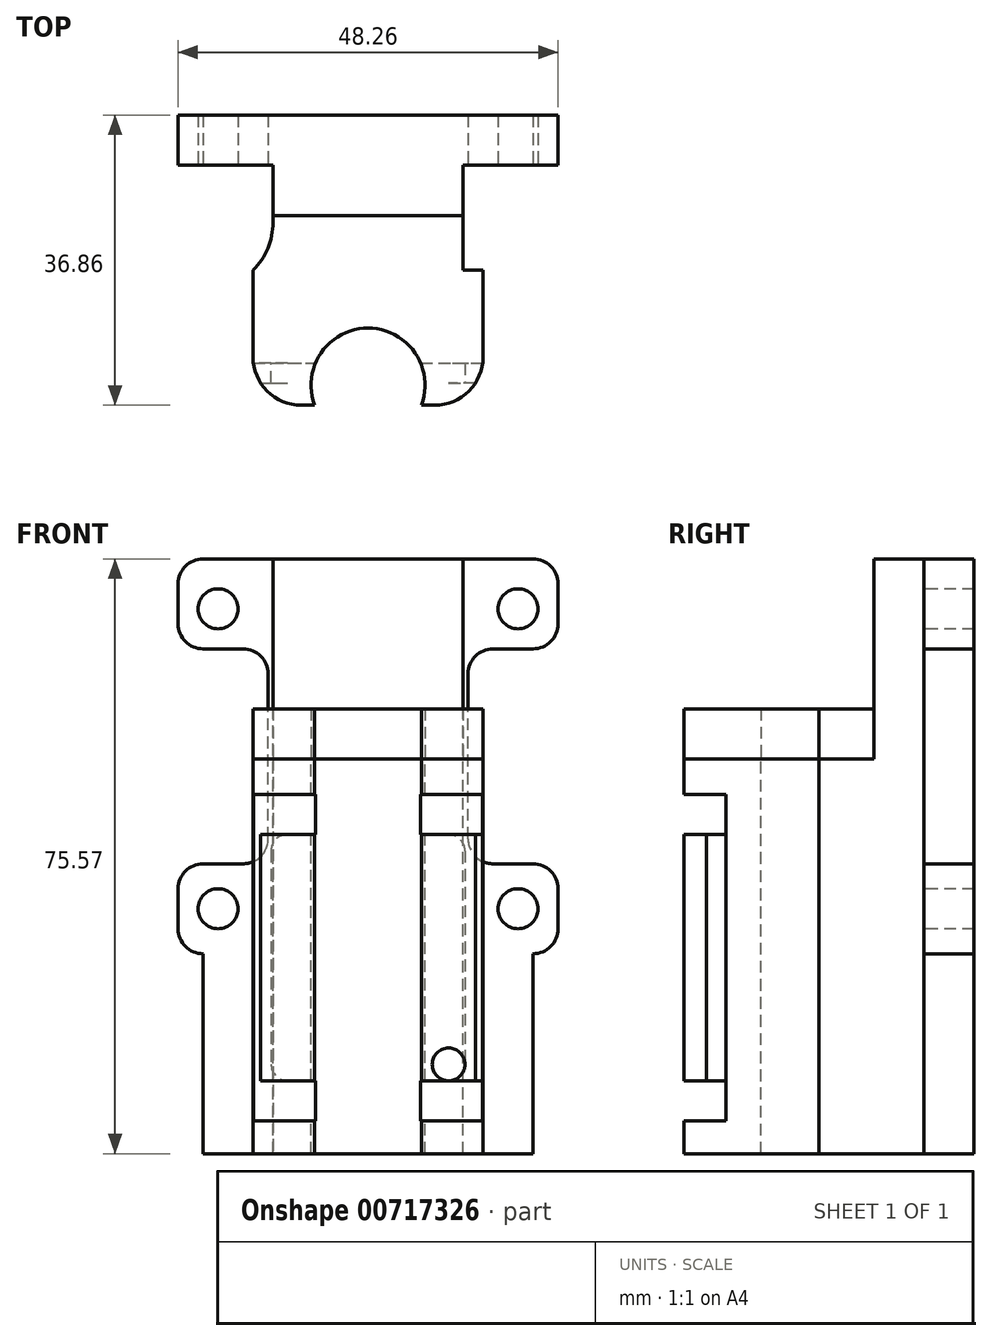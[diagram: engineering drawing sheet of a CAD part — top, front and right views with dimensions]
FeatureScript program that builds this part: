
annotation { "Feature Type Name" : "Feature", "Feature Type Description" : "" }
export const myFeature = defineFeature(function(context is Context, id is Id, definition is map)
    precondition{}
    {
        {
            var Q0;
            Q0=qCreatedBy(makeId("Front.planeOp"),FACE);
            var sketch = newSketch(context, id + "F0", { "sketchPlane" : qUnion([Q0])});
            skLineSegment(sketch, "E0.bottom", {"start": v(14.6, -25.4) * mm, "end": v(-14.6, -25.4) * mm});
            skLineSegment(sketch, "E0.top", {"start": v(14.6, 25.4) * mm, "end": v(-14.6, 25.4) * mm});
            skLineSegment(sketch, "E0.left", {"start": v(14.6, -25.4) * mm, "end": v(14.6, 25.4) * mm});
            skLineSegment(sketch, "E0.right", {"start": v(-14.6, -25.4) * mm, "end": v(-14.6, 25.4) * mm});
            skPoint(sketch, "E0.middle", {"position": v(0, 0) * mm});
            skSolve(sketch);
        }
        {
            var Q0;
            Q0=makeQuery(id+"F0.imprint","IMPRINT",FACE,{"disambiguationData":[TD([[makeQuery(id+"F0.imprint","IMPRINT",EDGE,{"derivedFrom":sQuery(id+"F0.wireOp",EDGE,"E0.bottom")}),-1.0]])]});
            extrude(context, id + "F1", {"entities" : qUnion([Q0]), "depth" : 1.65 * mm, "offsetDistance" : 25.4 * mm});
        }
        {
            var Q0;
            Q0=makeQuery(id+"F1.opExtrude","CAP_FACE",FACE,{"disambiguationData":[OSD([sQuery(id+"F0.wireOp",EDGE,"E0.bottom"),sQuery(id+"F0.wireOp",EDGE,"E0.top"),sQuery(id+"F0.wireOp",EDGE,"E0.left"),sQuery(id+"F0.wireOp",EDGE,"E0.right")])],"isStart":false});
            var sketch = newSketch(context, id + "F2", { "sketchPlane" : qUnion([Q0])});
            skLineSegment(sketch, "E1.bottom", {"start": v(14.6, -25.4) * mm, "end": v(-14.6, -25.4) * mm});
            skLineSegment(sketch, "E1.top", {"start": v(14.6, 25.4) * mm, "end": v(-14.6, 25.4) * mm});
            skLineSegment(sketch, "E1.left", {"start": v(14.6, -25.4) * mm, "end": v(14.6, 25.4) * mm});
            skLineSegment(sketch, "E1.right", {"start": v(-14.6, -25.4) * mm, "end": v(-14.6, 25.4) * mm});
            skPoint(sketch, "E1.middle", {"position": v(0, 0) * mm});
            skSolve(sketch);
        }
        {
            var Q0;
            Q0=qSketchRegion(id+"F2",true);
            extrude(context, id + "F3", {"entities" : qUnion([Q0]), "operationType" : NewBodyOperationType.ADD, "depth" : 5.33 * mm, "offsetDistance" : 25.4 * mm});
        }
        {
            var Q0;
            Q0=makeQuery(id+"F3.opExtrude","CAP_FACE",FACE,{"disambiguationData":[OSD([sQuery(id+"F2.wireOp",EDGE,"E1.bottom"),sQuery(id+"F2.wireOp",EDGE,"E1.top"),sQuery(id+"F2.wireOp",EDGE,"E1.left"),sQuery(id+"F2.wireOp",EDGE,"E1.right")])],"isStart":false});
            var sketch = newSketch(context, id + "F4", { "sketchPlane" : qUnion([Q0])});
            skLineSegment(sketch, "E2.bottom", {"start": v(14.6, -25.4) * mm, "end": v(-14.6, -25.4) * mm});
            skLineSegment(sketch, "E2.top", {"start": v(14.6, 25.4) * mm, "end": v(-14.6, 25.4) * mm});
            skLineSegment(sketch, "E2.left", {"start": v(14.6, -25.4) * mm, "end": v(14.6, 25.4) * mm});
            skLineSegment(sketch, "E2.right", {"start": v(-14.6, -25.4) * mm, "end": v(-14.6, 25.4) * mm});
            skPoint(sketch, "E2.middle", {"position": v(0, 0) * mm});
            skSolve(sketch);
        }
        {
            var Q0;
            Q0=makeQuery(id+"F4.imprint","IMPRINT",FACE,{"disambiguationData":[TD([[makeQuery(id+"F4.imprint","IMPRINT",EDGE,{"derivedFrom":sQuery(id+"F4.wireOp",EDGE,"E2.bottom")}),-1.0]])]});
            extrude(context, id + "F5", {"entities" : qUnion([Q0]), "operationType" : NewBodyOperationType.ADD, "depth" : 10.16 * mm, "offsetDistance" : 25.4 * mm});
        }
        {
            var Q0;
            Q0=makeQuery(id+"F5.boolean.opBoolean","MERGE",FACE,{"derivedFrom":[makeQuery(id+"F3.boolean.opBoolean","MERGE",FACE,{"derivedFrom":[makeQuery(id+"F1.opExtrude","SWEPT_FACE",FACE,{"disambiguationData":[OSD([sQuery(id+"F0.wireOp",EDGE,"E0.top")])]}),makeQuery(id+"F3.opExtrude","SWEPT_FACE",FACE,{"disambiguationData":[OSD([sQuery(id+"F2.wireOp",EDGE,"E1.top")])]})]}),makeQuery(id+"F5.opExtrude","SWEPT_FACE",FACE,{"disambiguationData":[OSD([sQuery(id+"F4.wireOp",EDGE,"E2.top")])]})]});
            var sketch = newSketch(context, id + "F6", { "sketchPlane" : qUnion([Q0])});
            skCircle(sketch, "E3", {"center": v(0, -14.59) * mm, "radius": 7.24 * mm});
            skSolve(sketch);
        }
        {
            var Q0;
            Q0=makeQuery(id+"F6.imprint","IMPRINT",FACE,{"disambiguationData":[TD([[makeQuery(id+"F6.imprint","IMPRINT",EDGE,{"derivedFrom":sQuery(id+"F6.wireOp",EDGE,"E3")}),1.0]])]});
            extrude(context, id + "F7", {"entities" : qUnion([Q0]), "operationType" : NewBodyOperationType.REMOVE, "oppositeDirection" : true, "depth" : 54.6 * mm, "offsetDistance" : 25.4 * mm});
        }
        {
            var Q0;
            Q0=makeQuery(id+"F5.opExtrude","CAP_EDGE",EDGE,{"disambiguationData":[OSD([sQuery(id+"F4.wireOp",EDGE,"E2.left")])],"isStart":false});
            var Q1;
            Q1=makeQuery(id+"F5.opExtrude","CAP_EDGE",EDGE,{"disambiguationData":[OSD([sQuery(id+"F4.wireOp",EDGE,"E2.right")])],"isStart":false});
            fillet(context, id + "F8", {"entities" : qUnion([Q0, Q1]), "radius" : 6.13 * mm, "tangentPropagation" : true, "allowEdgeOverflow" : false});
        }
        {
            var Q0;
            Q0=makeQuery(id+"F1.opExtrude","CAP_FACE",FACE,{"disambiguationData":[OSD([sQuery(id+"F0.wireOp",EDGE,"E0.bottom"),sQuery(id+"F0.wireOp",EDGE,"E0.top"),sQuery(id+"F0.wireOp",EDGE,"E0.left"),sQuery(id+"F0.wireOp",EDGE,"E0.right")])],"isStart":true});
            var sketch = newSketch(context, id + "F9", { "sketchPlane" : qUnion([Q0])});
            skLineSegment(sketch, "E4.bottom", {"start": v(-12.07, -25.4) * mm, "end": v(12.07, -25.4) * mm});
            skLineSegment(sketch, "E4.top", {"start": v(-12.07, 25.4) * mm, "end": v(12.07, 25.4) * mm});
            skLineSegment(sketch, "E4.left", {"start": v(-12.07, -25.4) * mm, "end": v(-12.07, 25.4) * mm});
            skLineSegment(sketch, "E4.right", {"start": v(12.07, -25.4) * mm, "end": v(12.07, 25.4) * mm});
            skPoint(sketch, "E4.middle", {"position": v(0, 0) * mm});
            skSolve(sketch);
        }
        {
            var Q0;
            Q0=makeQuery(id+"F9.imprint","IMPRINT",FACE,{"disambiguationData":[TD([[makeQuery(id+"F9.imprint","IMPRINT",EDGE,{"derivedFrom":sQuery(id+"F9.wireOp",EDGE,"E4.bottom")}),1.0]])]});
            extrude(context, id + "F10", {"entities" : qUnion([Q0]), "operationType" : NewBodyOperationType.ADD, "depth" : 13.36 * mm, "offsetDistance" : 25.4 * mm});
        }
        {
            var Q0;
            Q0=makeQuery(id+"F10.opExtrude","CAP_FACE",FACE,{"disambiguationData":[OSD([sQuery(id+"F0.wireOp",EDGE,"E0.bottom"),sQuery(id+"F0.wireOp",EDGE,"E0.top"),sQuery(id+"F0.wireOp",EDGE,"E0.left"),sQuery(id+"F0.wireOp",EDGE,"E0.right"),sQuery(id+"FqzVllP4adCt4uL_1.wireOp",EDGE,"rUKK4DPj-CFjB-32sL-ua7b-D3d8OQX9hJPr"),sQuery(id+"FqzVllP4adCt4uL_1.wireOp",EDGE,"QhqLk9Nw-JTsH-iBzY-8FqU-bG79tKQu5XAJ"),sQuery(id+"FqzVllP4adCt4uL_1.wireOp",EDGE,"1LGBsUpi-39JT-yavD-d9wK-DNn5E7mbPaeu"),sQuery(id+"FqzVllP4adCt4uL_1.wireOp",EDGE,"ZftcWFY4-HbeK-KcCb-HpW3-OdhueiSprC3Z"),sQuery(id+"F9.wireOp",EDGE,"E4.bottom"),sQuery(id+"F9.wireOp",EDGE,"E4.top"),sQuery(id+"F9.wireOp",EDGE,"E4.left"),sQuery(id+"F9.wireOp",EDGE,"E4.right")])],"isStart":false});
            var sketch = newSketch(context, id + "F11", { "sketchPlane" : qUnion([Q0])});
            skLineSegment(sketch, "E5", {"start": v(12.7, -25.4) * mm, "end": v(6.35, -25.4) * mm});
            skLineSegment(sketch, "E6", {"start": v(12.7, -25.4) * mm, "end": v(20.95, -25.4) * mm});
            skLineSegment(sketch, "E7", {"start": v(24.13, -22.23) * mm, "end": v(24.13, -17.14) * mm});
            skLineSegment(sketch, "E8", {"start": v(11.1, 24.77) * mm, "end": v(-11.12, 24.77) * mm});
            skLineSegment(sketch, "E9", {"start": v(-6.35, -25.4) * mm, "end": v(-12.7, -25.4) * mm});
            skLineSegment(sketch, "E10", {"start": v(-12.7, -25.4) * mm, "end": v(-20.96, -25.4) * mm});
            skLineSegment(sketch, "E11", {"start": v(-24.13, 21.59) * mm, "end": v(-24.13, 16.51) * mm});
            skLineSegment(sketch, "E12", {"start": v(-6.35, 8.9) * mm, "end": v(-6.35, -25.4) * mm});
            skLineSegment(sketch, "E13", {"start": v(-6.35, 24.77) * mm, "end": v(-6.35, 8.9) * mm});
            skLineSegment(sketch, "E14", {"start": v(6.35, 24.77) * mm, "end": v(6.35, 8.9) * mm});
            skLineSegment(sketch, "E15", {"start": v(6.35, -25.4) * mm, "end": v(6.35, 8.9) * mm});
            skLineSegment(sketch, "E16", {"start": v(-6.35, -25.4) * mm, "end": v(6.35, -25.4) * mm});
            skLineSegment(sketch, "E17", {"start": v(12.7, -10.8) * mm, "end": v(12.7, 10.16) * mm});
            skLineSegment(sketch, "E18", {"start": v(-12.7, -10.8) * mm, "end": v(-12.7, 10.16) * mm});
            skLineSegment(sketch, "E19", {"start": v(15.87, -13.97) * mm, "end": v(20.95, -13.97) * mm});
            skLineSegment(sketch, "E20", {"start": v(20.95, 13.34) * mm, "end": v(15.87, 13.34) * mm});
            skLineSegment(sketch, "E21", {"start": v(-15.88, -13.97) * mm, "end": v(-20.96, -13.97) * mm});
            skLineSegment(sketch, "E22", {"start": v(-15.88, 13.34) * mm, "end": v(-20.96, 13.34) * mm});
            skLineSegment(sketch, "E23", {"start": v(-24.13, -17.14) * mm, "end": v(-24.13, -22.23) * mm});
            skLineSegment(sketch, "E24", {"start": v(24.13, 21.59) * mm, "end": v(24.13, 16.51) * mm});
            skArc(sketch, "E25", {"start": v(-12.7, 10.16) * mm, "mid": v(-13.63, 12.4) * mm, "end": v(-15.88, 13.34) * mm});
            skArc(sketch, "E26", {"start": v(-15.88, -13.97) * mm, "mid": v(-13.63, -13.04) * mm, "end": v(-12.7, -10.8) * mm});
            skArc(sketch, "E27", {"start": v(15.87, 13.34) * mm, "mid": v(13.63, 12.4) * mm, "end": v(12.7, 10.16) * mm});
            skArc(sketch, "E28", {"start": v(12.7, -10.8) * mm, "mid": v(13.63, -13.04) * mm, "end": v(15.87, -13.97) * mm});
            skArc(sketch, "E29", {"start": v(24.13, 21.59) * mm, "mid": v(23.2, 23.84) * mm, "end": v(20.95, 24.77) * mm});
            skArc(sketch, "E30", {"start": v(20.95, 13.34) * mm, "mid": v(23.2, 14.26) * mm, "end": v(24.13, 16.51) * mm});
            skArc(sketch, "E31", {"start": v(24.13, -17.14) * mm, "mid": v(23.2, -14.9) * mm, "end": v(20.95, -13.97) * mm});
            skArc(sketch, "E32", {"start": v(20.95, -25.4) * mm, "mid": v(23.2, -24.47) * mm, "end": v(24.13, -22.23) * mm});
            skArc(sketch, "E33", {"start": v(-24.13, -22.23) * mm, "mid": v(-23.2, -24.47) * mm, "end": v(-20.96, -25.4) * mm});
            skArc(sketch, "E34", {"start": v(-20.96, -13.97) * mm, "mid": v(-23.2, -14.9) * mm, "end": v(-24.13, -17.14) * mm});
            skArc(sketch, "E35", {"start": v(-24.13, 16.51) * mm, "mid": v(-23.2, 14.26) * mm, "end": v(-20.96, 13.34) * mm});
            skArc(sketch, "E36", {"start": v(-20.96, 24.77) * mm, "mid": v(-23.2, 23.84) * mm, "end": v(-24.13, 21.59) * mm});
            skCircle(sketch, "E37", {"center": v(19.05, -19.69) * mm, "radius": 2.54 * mm});
            skCircle(sketch, "E38", {"center": v(-19.05, -19.69) * mm, "radius": 2.54 * mm});
            skCircle(sketch, "E39", {"center": v(-19.05, 18.41) * mm, "radius": 2.54 * mm});
            skCircle(sketch, "E40", {"center": v(19.05, 18.41) * mm, "radius": 2.54 * mm});
            skLineSegment(sketch, "E41", {"start": v(-11.12, -25.4) * mm, "end": v(-11.12, 24.77) * mm});
            skLineSegment(sketch, "E42", {"start": v(11.1, -25.4) * mm, "end": v(11.1, 24.77) * mm});
            skLineSegment(sketch, "E43", {"start": v(-20.96, 24.77) * mm, "end": v(-11.12, 24.77) * mm});
            skLineSegment(sketch, "E44", {"start": v(20.95, 24.77) * mm, "end": v(11.1, 24.77) * mm});
            skPoint(sketch, "E45", {"position": v(0, -25.4) * mm});
            skSolve(sketch);
        }
        {
            var Q0;
            Q0 = qSketchRegion(id + "F11", true);
            extrude(context, id + "F12", {"entities" : qUnion([Q0]), "operationType" : NewBodyOperationType.ADD, "depth" : 6.35 * mm, "offsetDistance" : 25.4 * mm});
        }
        {
            var Q0;
            Q0=makeQuery(id+"F10.boolean.opBoolean","MERGE",FACE,{"derivedFrom":[makeQuery(id+"F5.boolean.opBoolean","MERGE",FACE,{"derivedFrom":[makeQuery(id+"F3.boolean.opBoolean","MERGE",FACE,{"derivedFrom":[makeQuery(id+"F1.opExtrude","SWEPT_FACE",FACE,{"disambiguationData":[OSD([sQuery(id+"F0.wireOp",EDGE,"E0.top")])]}),makeQuery(id+"F3.opExtrude","SWEPT_FACE",FACE,{"disambiguationData":[OSD([sQuery(id+"F2.wireOp",EDGE,"E1.top")])]})]}),makeQuery(id+"F5.opExtrude","SWEPT_FACE",FACE,{"disambiguationData":[OSD([sQuery(id+"F4.wireOp",EDGE,"E2.top")])]})]}),makeQuery(id+"F10.opExtrude","SWEPT_FACE",FACE,{"disambiguationData":[OSD([sQuery(id+"F9.wireOp",EDGE,"E4.top")])]})]});
            extrude(context, id + "F13", {"entities" : qUnion([Q0]), "operationType" : NewBodyOperationType.REMOVE, "oppositeDirection" : true, "depth" : 0.63 * mm, "offsetDistance" : 25.4 * mm});
        }
        {
            var Q0;
            Q0=makeQuery(id+"F10.opExtrude","CAP_EDGE",EDGE,{"disambiguationData":[OSD([sQuery(id+"F9.wireOp",EDGE,"E4.left")])],"isStart":true});
            var Q1;
            Q1=makeQuery(id+"F10.opExtrude","CAP_EDGE",EDGE,{"disambiguationData":[OSD([sQuery(id+"F9.wireOp",EDGE,"E4.right")])],"isStart":true});
            fillet(context, id + "F14", {"entities" : qUnion([Q0, Q1]), "radius" : 8.58 * mm, "tangentPropagation" : true, "allowEdgeOverflow" : false});
        }
        {
            var Q0;
            Q0=makeQuery(id+"F12.boolean.opBoolean","MERGE",FACE,{"derivedFrom":[makeQuery(id+"F10.boolean.opBoolean","MERGE",FACE,{"derivedFrom":[makeQuery(id+"F5.boolean.opBoolean","MERGE",FACE,{"derivedFrom":[makeQuery(id+"F3.boolean.opBoolean","MERGE",FACE,{"derivedFrom":[makeQuery(id+"F1.opExtrude","SWEPT_FACE",FACE,{"disambiguationData":[OSD([sQuery(id+"F0.wireOp",EDGE,"E0.bottom")])]}),makeQuery(id+"F3.opExtrude","SWEPT_FACE",FACE,{"disambiguationData":[OSD([sQuery(id+"F2.wireOp",EDGE,"E1.bottom")])]})]}),makeQuery(id+"F5.opExtrude","SWEPT_FACE",FACE,{"disambiguationData":[OSD([sQuery(id+"F4.wireOp",EDGE,"E2.bottom")])]})]}),makeQuery(id+"F10.opExtrude","SWEPT_FACE",FACE,{"disambiguationData":[OSD([sQuery(id+"F9.wireOp",EDGE,"E4.bottom")])]})]}),makeQuery(id+"F12.opExtrude","SWEPT_FACE",FACE,{"disambiguationData":[OSD([sQuery(id+"F11.wireOp",EDGE,"E5"),sQuery(id+"F11.wireOp",EDGE,"E6"),sQuery(id+"F11.wireOp",EDGE,"E9"),sQuery(id+"F11.wireOp",EDGE,"E10"),sQuery(id+"F11.wireOp",EDGE,"E16")])]})]});
            extrude(context, id + "F15", {"entities" : qUnion([Q0]), "operationType" : NewBodyOperationType.ADD, "depth" : 25.4 * mm, "offsetDistance" : 25.4 * mm});
        }
        {
            var Q0;
            Q0=makeQuery(id+"F13.boolean.opBoolean","MERGE",FACE,{"derivedFrom":[makeQuery(id+"F12.opExtrude","SWEPT_FACE",FACE,{"disambiguationData":[OSD([sQuery(id+"F11.wireOp",EDGE,"E8"),sQuery(id+"F11.wireOp",EDGE,"E43"),sQuery(id+"F11.wireOp",EDGE,"E44")])]}),makeQuery(id+"F13.opExtrude","CAP_FACE",FACE,{"disambiguationData":[OSD([sQuery(id+"F0.wireOp",EDGE,"E0.top"),sQuery(id+"F2.wireOp",EDGE,"E1.top"),sQuery(id+"F4.wireOp",EDGE,"E2.top"),sQuery(id+"F9.wireOp",EDGE,"E4.top")])],"isStart":false})]});
            var sketch = newSketch(context, id + "F16", { "sketchPlane" : qUnion([Q0])});
            skLineSegment(sketch, "E46.bottom", {"start": v(-22.36, -19.22) * mm, "end": v(24.35, -19.22) * mm});
            skLineSegment(sketch, "E46.top", {"start": v(-22.36, 6.96) * mm, "end": v(24.35, 6.96) * mm});
            skLineSegment(sketch, "E46.left", {"start": v(-22.36, -19.22) * mm, "end": v(-22.36, 6.96) * mm});
            skLineSegment(sketch, "E46.right", {"start": v(24.35, -19.22) * mm, "end": v(24.35, 6.96) * mm});
            skSolve(sketch);
        }
        {
            var Q0;
            Q0 = qSketchRegion(id + "F16", true);
            extrude(context, id + "F17", {"entities" : qUnion([Q0]), "operationType" : NewBodyOperationType.REMOVE, "oppositeDirection" : true, "depth" : 25.4 * mm, "offsetDistance" : 25.4 * mm});
        }
        {
            var Q0;
            {var subQ2=makeQuery(id+"F1.opExtrude","SWEPT_FACE",FACE,{"disambiguationData":[OSD([sQuery(id+"F0.wireOp",EDGE,"E0.left")])]});var subQ5=sQuery(id+"F4.wireOp",EDGE,"E2.bottom");var subQ7=sQuery(id+"F4.wireOp",EDGE,"E2.left");var subQ8=sQuery(id+"F4.wireOp",EDGE,"E2.top");var subQ9=makeQuery(id+"F5.opExtrude","CAP_FACE",FACE,{"disambiguationData":[OSD([subQ5,subQ8,subQ7,sQuery(id+"F4.wireOp",EDGE,"E2.right")])],"isStart":false});Q0=makeQuery(id+"F15.boolean.opBoolean","MERGE",FACE,{"derivedFrom":[makeQuery(id+"F7.boolean.opBoolean","SPLIT",FACE,{"disambiguationData":[TD([subQ2])],"derivedFrom":subQ9}),makeQuery(id+"F15.opExtrude","SWEPT_FACE",FACE,{"disambiguationData":[OSD([subQ5]),TDD([makeQuery(id+"F7.boolean.opBoolean","SPLIT",EDGE,{"disambiguationData":[TD([subQ2])],"derivedFrom":makeQuery(id+"F5.opExtrude","CAP_EDGE",EDGE,{"disambiguationData":[OSD([subQ5])],"isStart":false})})])]})]});}
            var sketch = newSketch(context, id + "F18", { "sketchPlane" : qUnion([Q0])});
            skLineSegment(sketch, "E47.bottom", {"start": v(-21.88, -5.17) * mm, "end": v(21.74, -5.17) * mm});
            skLineSegment(sketch, "E47.top", {"start": v(-21.88, -10.25) * mm, "end": v(21.74, -10.25) * mm});
            skLineSegment(sketch, "E47.left", {"start": v(-21.88, -5.17) * mm, "end": v(-21.88, -10.25) * mm});
            skLineSegment(sketch, "E47.right", {"start": v(21.74, -5.17) * mm, "end": v(21.74, -10.25) * mm});
            skPoint(sketch, "E47.middle", {"position": v(-0.07, -7.7) * mm});
            skLineSegment(sketch, "E48.bottom", {"start": v(-21.88, -41.54) * mm, "end": v(21.74, -41.54) * mm});
            skLineSegment(sketch, "E48.top", {"start": v(-21.88, -46.62) * mm, "end": v(21.74, -46.62) * mm});
            skLineSegment(sketch, "E48.left", {"start": v(-21.88, -41.54) * mm, "end": v(-21.88, -46.62) * mm});
            skLineSegment(sketch, "E48.right", {"start": v(21.74, -41.54) * mm, "end": v(21.74, -46.62) * mm});
            skPoint(sketch, "E48.middle", {"position": v(-0.07, -44.08) * mm});
            skSolve(sketch);
        }
        {
            var Q0;
            Q0 = qSketchRegion(id + "F18", true);
            extrude(context, id + "F19", {"entities" : qUnion([Q0]), "operationType" : NewBodyOperationType.REMOVE, "oppositeDirection" : true, "depth" : 5.33 * mm, "offsetDistance" : 25.4 * mm});
        }
        {
            var Q0;
            {var subQ0=sQuery(id+"F4.wireOp",EDGE,"E2.right");var subQ1=sQuery(id+"F2.wireOp",EDGE,"E1.right");var subQ2=sQuery(id+"F0.wireOp",EDGE,"E0.right");Q0=makeQuery(id+"F15.boolean.opBoolean","MERGE",FACE,{"derivedFrom":[makeQuery(id+"F5.boolean.opBoolean","MERGE",FACE,{"derivedFrom":[makeQuery(id+"F3.boolean.opBoolean","MERGE",FACE,{"derivedFrom":[makeQuery(id+"F1.opExtrude","SWEPT_FACE",FACE,{"disambiguationData":[OSD([subQ2])]}),makeQuery(id+"F3.opExtrude","SWEPT_FACE",FACE,{"disambiguationData":[OSD([subQ1])]})]}),makeQuery(id+"F5.opExtrude","SWEPT_FACE",FACE,{"disambiguationData":[OSD([subQ0])]})]}),makeQuery(id+"F15.opExtrude","SWEPT_FACE",FACE,{"disambiguationData":[OSD([sQuery(id+"F0.wireOp",EDGE,"E0.bottom"),subQ2,sQuery(id+"F2.wireOp",EDGE,"E1.bottom"),subQ1,sQuery(id+"F4.wireOp",EDGE,"E2.bottom"),subQ0])]})]});}
            var sketch = newSketch(context, id + "F20", { "sketchPlane" : qUnion([Q0])});
            skLineSegment(sketch, "E49.bottom", {"start": v(11.82, -10.2) * mm, "end": v(14.3, -10.2) * mm});
            skLineSegment(sketch, "E49.top", {"start": v(11.82, -41.74) * mm, "end": v(14.3, -41.74) * mm});
            skLineSegment(sketch, "E49.left", {"start": v(11.82, -10.2) * mm, "end": v(11.82, -41.74) * mm});
            skLineSegment(sketch, "E49.right", {"start": v(14.3, -10.2) * mm, "end": v(14.3, -41.74) * mm});
            skSolve(sketch);
        }
        {
            var Q0;
            Q0 = qSketchRegion(id + "F20", true);
            extrude(context, id + "F21", {"entities" : qUnion([Q0]), "operationType" : NewBodyOperationType.REMOVE, "oppositeDirection" : true, "depth" : 2.3 * mm, "offsetDistance" : 25.4 * mm});
        }
        {
            var Q0;
            {var subQ0=sQuery(id+"F4.wireOp",EDGE,"E2.left");var subQ1=sQuery(id+"F2.wireOp",EDGE,"E1.left");var subQ2=sQuery(id+"F0.wireOp",EDGE,"E0.left");Q0=makeQuery(id+"F15.boolean.opBoolean","MERGE",FACE,{"derivedFrom":[makeQuery(id+"F5.boolean.opBoolean","MERGE",FACE,{"derivedFrom":[makeQuery(id+"F3.boolean.opBoolean","MERGE",FACE,{"derivedFrom":[makeQuery(id+"F1.opExtrude","SWEPT_FACE",FACE,{"disambiguationData":[OSD([subQ2])]}),makeQuery(id+"F3.opExtrude","SWEPT_FACE",FACE,{"disambiguationData":[OSD([subQ1])]})]}),makeQuery(id+"F5.opExtrude","SWEPT_FACE",FACE,{"disambiguationData":[OSD([subQ0])]})]}),makeQuery(id+"F15.opExtrude","SWEPT_FACE",FACE,{"disambiguationData":[OSD([sQuery(id+"F0.wireOp",EDGE,"E0.bottom"),subQ2,sQuery(id+"F2.wireOp",EDGE,"E1.bottom"),subQ1,sQuery(id+"F4.wireOp",EDGE,"E2.bottom"),subQ0])]})]});}
            var sketch = newSketch(context, id + "F22", { "sketchPlane" : qUnion([Q0])});
            skLineSegment(sketch, "E50.bottom", {"start": v(-14.31, -10.05) * mm, "end": v(-11.83, -10.05) * mm});
            skLineSegment(sketch, "E50.top", {"start": v(-14.31, -41.58) * mm, "end": v(-11.83, -41.58) * mm});
            skLineSegment(sketch, "E50.left", {"start": v(-14.31, -10.05) * mm, "end": v(-14.31, -41.58) * mm});
            skLineSegment(sketch, "E50.right", {"start": v(-11.83, -10.05) * mm, "end": v(-11.83, -41.58) * mm});
            skSolve(sketch);
        }
        {
            var Q0;
            Q0 = qSketchRegion(id + "F22", true);
            extrude(context, id + "F23", {"entities" : qUnion([Q0]), "operationType" : NewBodyOperationType.REMOVE, "oppositeDirection" : true, "depth" : 2.3 * mm, "offsetDistance" : 25.4 * mm});
        }
        {
            var Q0;
            {var subQ4=sQuery(id+"F4.wireOp",EDGE,"E2.left");var subQ7=sQuery(id+"F18.wireOp",EDGE,"E47.top");Q0=makeQuery(id+"F23.boolean.opBoolean","INTERSECT",EDGE,{"derivedFrom":[makeQuery(id+"F19.boolean.opBoolean","COPY",FACE,{"disambiguationData":[TD([makeQuery(id+"F8.opFillet","BLEND_FACE",FACE,{"disambiguationData":[OSD([subQ4])]})])],"derivedFrom":makeQuery(id+"F19.opExtrude","SWEPT_FACE",FACE,{"disambiguationData":[OSD([subQ7])]})}),makeQuery(id+"F23.opExtrude","CAP_FACE",FACE,{"disambiguationData":[OSD([sQuery(id+"F22.wireOp",EDGE,"E50.bottom"),sQuery(id+"F22.wireOp",EDGE,"E50.top"),sQuery(id+"F22.wireOp",EDGE,"E50.left"),sQuery(id+"F22.wireOp",EDGE,"E50.right")])],"isStart":false})]});}
            var Q1;
            {var subQ5=sQuery(id+"F4.wireOp",EDGE,"E2.right");var subQ7=sQuery(id+"F18.wireOp",EDGE,"E47.top");Q1=makeQuery(id+"F21.boolean.opBoolean","INTERSECT",EDGE,{"derivedFrom":[makeQuery(id+"F19.boolean.opBoolean","COPY",FACE,{"disambiguationData":[TD([makeQuery(id+"F8.opFillet","BLEND_FACE",FACE,{"disambiguationData":[OSD([subQ5])]})])],"derivedFrom":makeQuery(id+"F19.opExtrude","SWEPT_FACE",FACE,{"disambiguationData":[OSD([subQ7])]})}),makeQuery(id+"F21.opExtrude","CAP_FACE",FACE,{"disambiguationData":[OSD([sQuery(id+"F20.wireOp",EDGE,"E49.bottom"),sQuery(id+"F20.wireOp",EDGE,"E49.top"),sQuery(id+"F20.wireOp",EDGE,"E49.left"),sQuery(id+"F20.wireOp",EDGE,"E49.right")])],"isStart":false})]});}
            var Q2;
            {var subQ5=sQuery(id+"F4.wireOp",EDGE,"E2.right");var subQ7=sQuery(id+"F18.wireOp",EDGE,"E48.bottom");Q2=makeQuery(id+"F21.boolean.opBoolean","INTERSECT",EDGE,{"derivedFrom":[makeQuery(id+"F19.boolean.opBoolean","COPY",FACE,{"disambiguationData":[TD([makeQuery(id+"F8.opFillet","BLEND_FACE",FACE,{"disambiguationData":[OSD([subQ5])]})])],"derivedFrom":makeQuery(id+"F19.opExtrude","SWEPT_FACE",FACE,{"disambiguationData":[OSD([subQ7])]})}),makeQuery(id+"F21.opExtrude","CAP_FACE",FACE,{"disambiguationData":[OSD([sQuery(id+"F20.wireOp",EDGE,"E49.bottom"),sQuery(id+"F20.wireOp",EDGE,"E49.top"),sQuery(id+"F20.wireOp",EDGE,"E49.left"),sQuery(id+"F20.wireOp",EDGE,"E49.right")])],"isStart":false})]});}
            var Q3;
            {var subQ4=sQuery(id+"F4.wireOp",EDGE,"E2.left");var subQ6=sQuery(id+"F18.wireOp",EDGE,"E48.bottom");Q3=makeQuery(id+"F23.boolean.opBoolean","INTERSECT",EDGE,{"derivedFrom":[makeQuery(id+"F19.boolean.opBoolean","COPY",FACE,{"disambiguationData":[TD([makeQuery(id+"F8.opFillet","BLEND_FACE",FACE,{"disambiguationData":[OSD([subQ4])]})])],"derivedFrom":makeQuery(id+"F19.opExtrude","SWEPT_FACE",FACE,{"disambiguationData":[OSD([subQ6])]})}),makeQuery(id+"F23.opExtrude","CAP_FACE",FACE,{"disambiguationData":[OSD([sQuery(id+"F22.wireOp",EDGE,"E50.bottom"),sQuery(id+"F22.wireOp",EDGE,"E50.top"),sQuery(id+"F22.wireOp",EDGE,"E50.left"),sQuery(id+"F22.wireOp",EDGE,"E50.right")])],"isStart":false})]});}
            fillet(context, id + "F24", {"entities" : qUnion([Q0, Q1, Q2, Q3]), "radius" : 2.08 * mm, "tangentPropagation" : true, "allowEdgeOverflow" : false});
        }
        {
            var Q0;
            Q0=makeQuery(id+"F17.boolean.opBoolean","COPY",FACE,{"derivedFrom":makeQuery(id+"F17.opExtrude","CAP_FACE",FACE,{"disambiguationData":[OSD([sQuery(id+"F16.wireOp",EDGE,"E46.bottom"),sQuery(id+"F16.wireOp",EDGE,"E46.top"),sQuery(id+"F16.wireOp",EDGE,"E46.left"),sQuery(id+"F16.wireOp",EDGE,"E46.right")])],"isStart":false})});
            extrude(context, id + "F25", {"entities" : qUnion([Q0]), "depth" : 6.35 * mm, "offsetDistance" : 25.4 * mm});
        }
    });
